# Revit family: svetovye tekhnologii_svetilnik arctic_opl_eco_led_1200_4000k
name_source: partatom
category: Осветительные приборы
revit_build: Autodesk Revit 2018 (Build: 20170927_1515(x64)
units: mm (PartAtom-declared; Revit-internal decimal feet)

## family parameters
Источник света = Да
Общий = Да
Основа = Грань
При загрузке вырезать с полостями = Нет
Размер круглого соединителя = Использовать диаметр
Тип детали = Нормальный
Точка расчета площади = Нет

## types (1)
- ARCTIC.OPL ECO LED 1200
    n_фаз = 1
    Высота светильника = 110 мм
    Длина верха = 1268 мм
    Длина светильника = 1278 мм
    Единица измерения = шт.
    Завод изготовитель = Световые Технологии
    Код оборудования = 1088000100
    Кол. ламп = 0
    Количество фаз = 1
    Коэффициент мощности = 0.96
    Марка = ARCTIC.OPL ECO LED 1200
    Марка светильника = ARCTIC.OPL ECO LED 1200
    Материал = Пластмасса
    Материал1 = Стекло
    Мощность_1_лампы_светильника_Вт = 46
    Наименование = Светильник с люминесцетными лампами 2х36 Вт, крепление на поверхность потолка; конструкция: корпус из АБС-пластика, рассеиватель из полистирола, в корпусе установлена пускорегулирующая аппаратура; степень защиты IP65
    Напряжение = 230 В
    Номинальная мощность = 0.0 кВт
    О_ЕдиницыИзмерения = шт.
    Отметка по умолчанию = 1500 мм
    Полная мощность = 0.0 кВт
    Полная установленная мощность = 0.0 кВт
    Сальник = 639 мм
    Светофильтр = 16777215
    Смещение цветовой температуры при затухании лампы = <Нет>
    Сортировка в спецификации по разделам = II. ЭЛЕКТРООСВЕТИТЕЛЬНЫЕ ПРИБОРЫ,  ИСТОЧНИКИ СВЕТА, СИГНАЛЬНЫЕ ЗНАКИ.
    Ток = 0 А
    Угол наклона = -90.00°
    Файл фотометрической сетки = arctic_opl_eco_led_1200_4000k.ies
    Ширина верха = 160 мм
    Ширина светильника = 170 мм
    короткое наименование = ARCTIC.OPL ECO LED 1200

## geometry (parser evidence)
native form markers: Blend x2
no freeform markers — native parametric forms only
